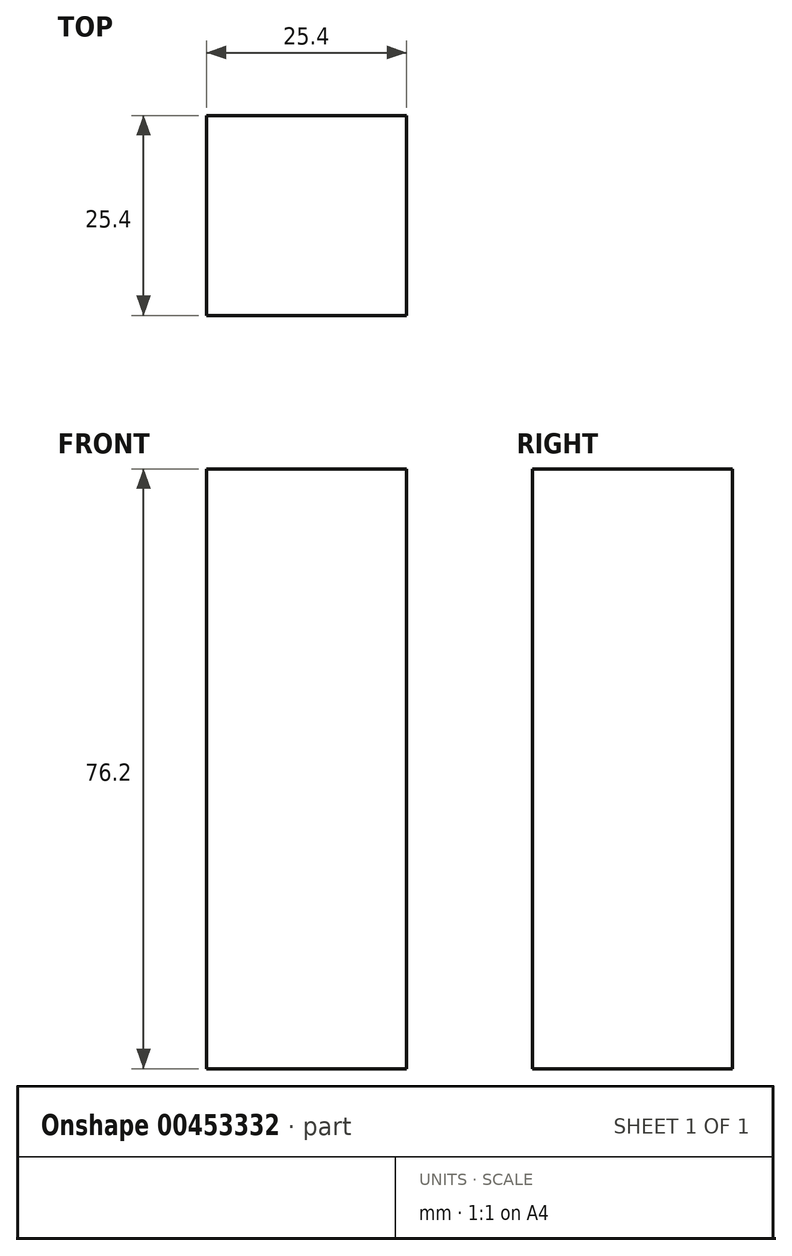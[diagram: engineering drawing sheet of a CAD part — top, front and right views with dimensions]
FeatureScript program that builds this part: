
annotation { "Feature Type Name" : "Feature", "Feature Type Description" : "" }
export const myFeature = defineFeature(function(context is Context, id is Id, definition is map)
    precondition{}
    {
        {
            var Q0;
            Q0=qCreatedBy(makeId("Front.planeOp"),FACE);
            var sketch = newSketch(context, id + "F0", { "sketchPlane" : qUnion([Q0])});
            skLineSegment(sketch, "E0.bottom", {"start": v(-12.7, 38.1) * mm, "end": v(12.7, 38.1) * mm});
            skLineSegment(sketch, "E0.top", {"start": v(-12.7, -38.1) * mm, "end": v(12.7, -38.1) * mm});
            skLineSegment(sketch, "E0.left", {"start": v(-12.7, 38.1) * mm, "end": v(-12.7, -38.1) * mm});
            skLineSegment(sketch, "E0.right", {"start": v(12.7, 38.1) * mm, "end": v(12.7, -38.1) * mm});
            skPoint(sketch, "E0.middle", {"position": v(0, 0) * mm});
            skSolve(sketch);
        }
        {
            var Q0;
            Q0 = qSketchRegion(id + "F0", true);
            extrude(context, id + "F1", {"entities" : qUnion([Q0]), "depth" : 25.4 * mm});
        }
    });
